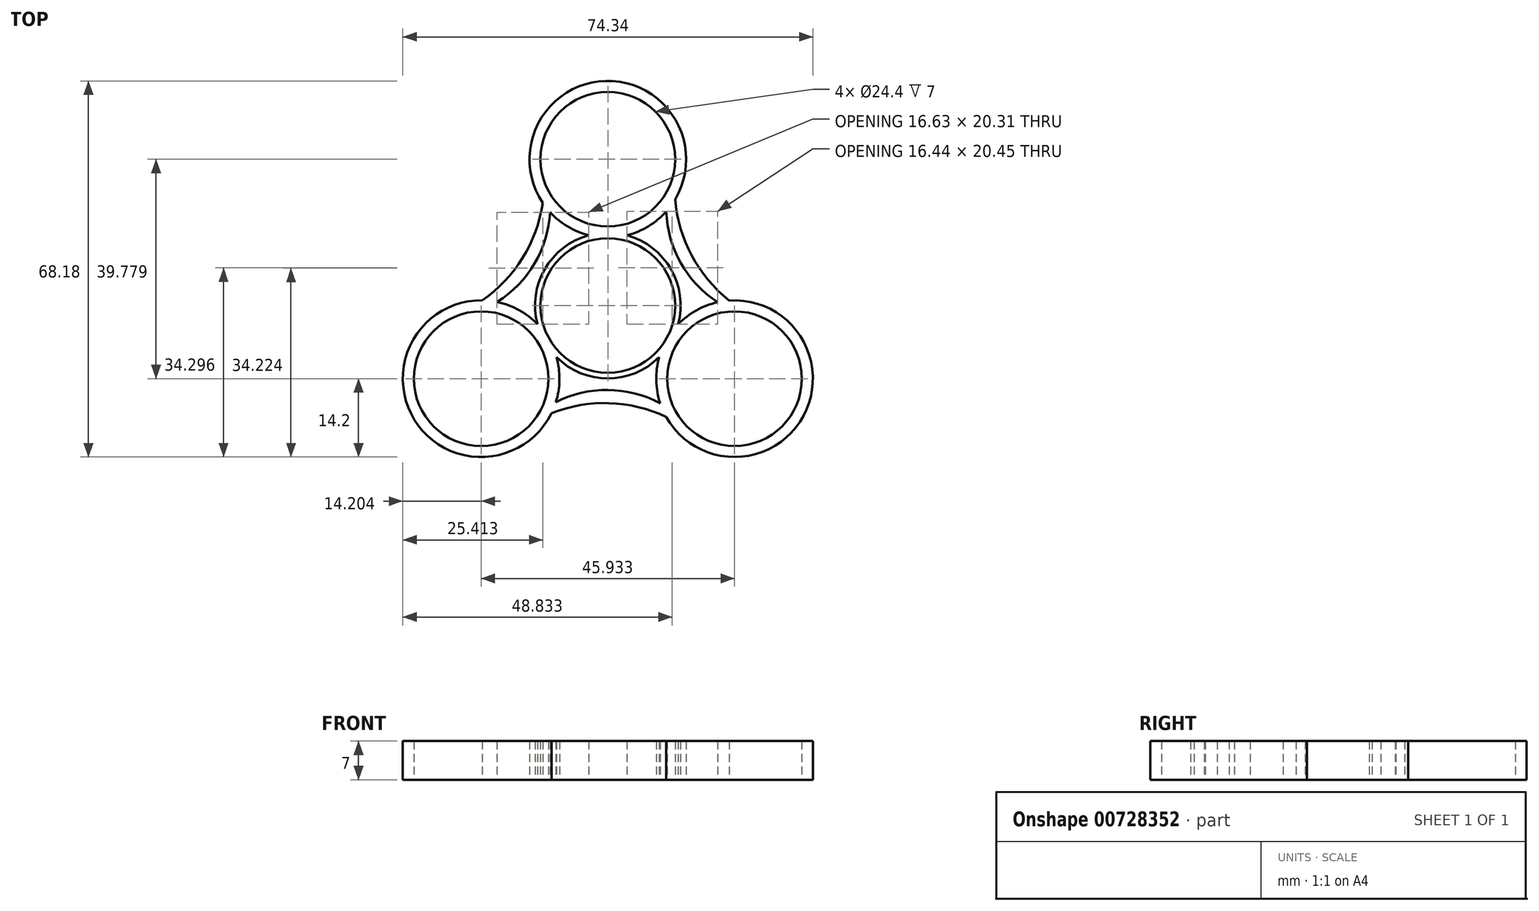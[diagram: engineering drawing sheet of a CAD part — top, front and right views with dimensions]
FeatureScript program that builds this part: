
annotation { "Feature Type Name" : "Feature", "Feature Type Description" : "" }
export const myFeature = defineFeature(function(context is Context, id is Id, definition is map)
    precondition{}
    {
        {
            var Q0;
            Q0=qCreatedBy(makeId("Top.planeOp"),FACE);
            var sketch = newSketch(context, id + "F0", { "sketchPlane" : qUnion([Q0])});
            skCircle(sketch, "E0", {"center": v(0, 0) * mm, "radius": 12.2 * mm});
            skCircle(sketch, "E1", {"center": v(0, 26.52) * mm, "radius": 12.2 * mm});
            skCircle(sketch, "E2.1.0", {"center": v(-22.97, -13.26) * mm, "radius": 12.2 * mm});
            skCircle(sketch, "E2.2.0", {"center": v(22.97, -13.26) * mm, "radius": 12.2 * mm});
            skArc(sketch, "E3", {"start": v(-3.44, 12.74) * mm, "mid": v(-11.43, 6.6) * mm, "end": v(-12.76, -3.39) * mm});
            skArc(sketch, "E4", {"start": v(3.44, 12.74) * mm, "mid": v(0, 40.72) * mm, "end": v(-3.44, 12.74) * mm});
            skArc(sketch, "E5.1.0", {"start": v(-12.76, -3.39) * mm, "mid": v(-35.26, -20.36) * mm, "end": v(-9.31, -9.35) * mm});
            skArc(sketch, "E5.2.0", {"start": v(9.31, -9.35) * mm, "mid": v(35.26, -20.36) * mm, "end": v(12.76, -3.39) * mm});
            skArc(sketch, "E6.trimOffspring", {"start": v(-9.31, -9.35) * mm, "mid": v(0, -13.2) * mm, "end": v(9.31, -9.35) * mm});
            skArc(sketch, "E7.trimOffspring", {"start": v(12.76, -3.39) * mm, "mid": v(11.43, 6.6) * mm, "end": v(3.44, 12.74) * mm});
            skArc(sketch, "E8", {"start": v(-20.07, 0.64) * mm, "mid": v(-13.28, 7.6) * mm, "end": v(-10.46, 16.92) * mm});
            skArc(sketch, "E9", {"start": v(-22.77, 0.94) * mm, "mid": v(-15.44, 8.64) * mm, "end": v(-11.8, 18.62) * mm});
            skArc(sketch, "E10.1.0", {"start": v(10.57, -20.18) * mm, "mid": v(0.24, -17.7) * mm, "end": v(-10.22, -19.53) * mm});
            skArc(sketch, "E10.1.1", {"start": v(9.48, -17.7) * mm, "mid": v(0.05, -15.3) * mm, "end": v(-9.42, -17.52) * mm});
            skArc(sketch, "E10.2.0", {"start": v(12.2, 19.25) * mm, "mid": v(15.2, 9.05) * mm, "end": v(22.02, 0.9) * mm});
            skArc(sketch, "E10.2.1", {"start": v(10.6, 17.06) * mm, "mid": v(13.23, 7.7) * mm, "end": v(19.88, 0.6) * mm});
            skSolve(sketch);
        }
        {
            var Q0;
            Q0 = qSketchRegion(id + "F0", true);
            extrude(context, id + "F1", {"entities" : qUnion([Q0]), "depth" : 7 * mm, "offsetDistance" : 25 * mm});
        }
    });
